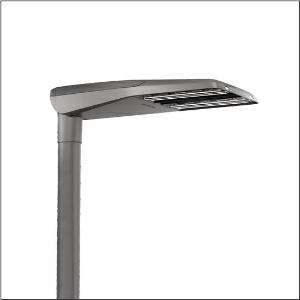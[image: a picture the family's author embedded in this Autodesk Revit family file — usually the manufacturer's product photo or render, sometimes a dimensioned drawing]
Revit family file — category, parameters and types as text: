
# Revit family: streetlight_sl_11_iq_midi___pc-r_5xc3f11g08me_10ab
name_source: partatom
category: Lighting Fixtures
units: mm (PartAtom-declared; Revit-internal decimal feet)

## family parameters
Cut with Voids When Loaded = No
Host = Face
Light Source = No
Part Type = Normal
Room Calculation Point = No
Round Connector Dimension = Use Diameter
Shared = No

## types (1)
- --- (1 x LED, 9590 lm, 124.5 W, 1800K)
    Apparent Load = 125 VA
    CIE Flux Codes = 37 73 96 100 100
    Color Rendering = 70
    Color Temperature = 1800K
    Default Elevation = 1800 mm  [stored 5.90551 ft]
    Description = Streetlight SL 11 iQ midi, mast luminaire, primary light control with 3 zone facetted reflector, of plastic, silver coated, highly specular, primary optical cover: cover, of PMMA, transparent, light distribution: PC-R, light emission: direct distribution, primary light characteristic: asymmetric, right, installation type: post-top, side-entry, LED, High Power LED, rated luminous flux: 9.590lm, luminous efficacy: 77lm/W, light colour: 718, colour temperature: 1800K, control: Street-Remote, Auto-Match, Temp-Guard, Lumen-Switch, Night-Set, Smart-Wire, Light-Fading, Desk-Remote (wireless, voltage-free reading and setting of iQ features in the workshop via application-optimized NFC function/RFID function), optimised constant luminous flux control (CLO 2.0), presetting dimming linear, with cable H07RN-F 5x 1.5mm², mains connection: 230..240V, AC, 50/60Hz, connection cable pre-assembled, cable length: 12,5m, start of lifetime: 125W, end of service life: 132W, reduction: 55W, luminaire housing, of diecast aluminium, powder-coated, Siteco® metallic grey (DB 702S), please order mast flange separately, inclination adjustable without tools: 0°, 5°, 10°, 15° (post-top) | 0°, -5°, -10°, -15° (side-entry), sealing non-destructively replaceable, multi-level sealing system, length: 780mm, width: 376mm, height: 118mm, mast flange for spigot size: 42mm (side-entry): 5XC10008XM4, 60/48mm (side-entry/post-top): 5XC10108XM2, 76/60mm (side-entry/post-top): 5XC10108XM1, equipment: Power, protection rating (complete): IP66, insulation class (complete): insulation class II (safety insulation), certification: CE, ENEC, VDE, impact resistance: IK09, permissible operating ambient temperature for outdoor applications: -25..+50°C, standard-compliant lighting for roads and squares, Environmental Product Declaration (EPD) tested and certified by an independent institute, packaging unit: 1 piece

Light Distribution: PC-R
    Height = 118 mm
    Lamp = 1 x LED
    Lamp Light Flux = 9590 lm
    Lamp Power = 124.5 W
    Lamp count = 1
    Length = 780 mm
    Luminous efficacy = 77 lm/W
    Manufacturer = Siteco
    ModVariant = No
    Model = 5XC3F11G08ME
    Number of Poles = 1
    OnlyDefault = Yes
    Power Factor = 1
    Product Name = Streetlight SL 11 iQ midi | PC-R
    Product group = mast luminaire | pylon top
    ProductGroupID = 6100
    Protection Class = Protection class II
    Protection Degree = IP 66
    RLX_Detail_Level = 1
    RLX_Emergency_Light_Flux = 0 lm
    RLX_Emergency_Type = 0
    RLX_Emergency_Type_DB = No
    RlxData = <blob elided: 74557 chars, md5=339c1e16>
    Socket = socket
    Standby Power = 0 W
    System Light Flux = 9590 lm
    System Power = 125 W
    Type Comments = factory setting: luminous flux: 100 % | dim-lin: 254 | 554 mA
    Type Image = l_1005960.jpg
    URL = http://relux.com
    VarID = @adj_009929
    Voltage = 0 V
    Weight = 0.00 kg
    Width = 376 mm

note: [stored X ft] marks values corroborated as IEEE doubles in the binary element streams (Revit-internal decimal feet)

## geometry (parser evidence)
native form markers: Blend x4, Sweep x12
no freeform markers — native parametric forms only
